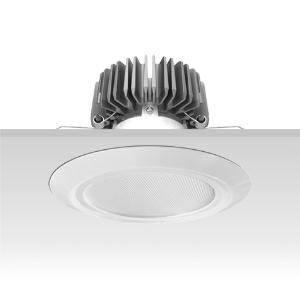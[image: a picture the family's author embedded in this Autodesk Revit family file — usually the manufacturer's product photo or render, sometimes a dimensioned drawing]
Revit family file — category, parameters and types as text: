
# Revit family: 3f_filippi_-_3f_reno_bianco_ampio_3f_filippi_-_30675_a01037_-_3f_reno_200_wh_2000-930_dali_wide___vs_wh_e44b
name_source: partatom
category: Lighting Fixtures
units: mm (PartAtom-declared; Revit-internal decimal feet)

## family parameters
Cut with Voids When Loaded = No
Host = Face
Light Source = No
Part Type = Normal
Room Calculation Point = No
Round Connector Dimension = Use Diameter
Shared = No

## types (1)
- 3F Filippi - 3F Reno Bianco Ampio (1 x LED, 1650 lm, 24 W, 3000 K)
    Apparent Load = 24 VA
    Approval mark = CE
    CIE Flux Codes = 75 94 99 100 100
    Color Rendering = 90
    Color Temperature = 3000 K
    Control Gear = Electronic transformer
    Default Elevation = 1800 mm
    Description = ILLUMINOTECHNICAL
Luminous efficiency 100% (DLOR 100%, ULOR 0%).
Initial luminous flux of the luminaire 1650 lm.
Direct symmetric wide distribution.
Installation Interdistance Transv.D = 1.16 x hu - Long.D = 1.14 x hu.
Average luminance <3000 cd/m² for radial angles >65°.
Tabular UGR (CIE 117 - 4H-8H; S=0.25H; 70/50/20): RUG 20.3 - 20.2.
Beam angle: 74° - 74°.
Luminous efficacy 69 lm/W.
Lifetime (L90/B10): 30000 h. (tq+25°C)
Lifetime (L85/B10): 50000 h. (tq+25°C)
Lifetime (L70/B10): 80000 h. (tq+25°C)
Sudden decreased luminous flux after 50000 hours: 0% (C0).
Photobiological safety in compliance with IEC/TR 62778: RG0 risk exempt, (IEC 62471).
In compliance with IEC/EN 62722-2-1 - IEC/EN 62717 standards.

SOURCE
Compact LED module 2000/930.
Energy efficiency class (UE 2019/2020 - UE 2019/2015): E.
CIE 13.3 Colour rendering index: CRI >90 (R9 >50%).
IES TM-30 Fidelity Index: Rf = 92 Rg = 101.
CCT nominal colour temperature 3000 K.
Colour initial tolerance (MacAdam): SDCM 3.
Zhaga Book 3 compliant.

MECHANICAL
Passive heat dissipator in die-casting aluminium, oversized, for optimum thermal management of the LED module.
Parabolic element with graduated/concentric rings in white polycarbonate.
Transparent external lens with glossy and satin differentiated surfaces, with a cooling and anti-insect system in methacrylate (PMMA).
Fastening spring clips in stainless steel.
Dimensions: diameter 226 mm, height 146 mm. Weight 1.195 kg.
IP44 protection degree for exposed part, IP20 for recessed part.
Mechanical strength to impacts IK06 (1 joule).
Glow-wire test resistance 650°C.

ELECTRICAL
Wiring on a separate unit.
Halogen Free DALI-2 DATI (Parts 251, 252, 253), PUSH-DIM, electronic wiring 230V-50/60Hz, power factor 0.95 at full load, THD <25%, constant output current, SELV, class II, 1 driver, 1 DALI addresse.
Power of the luminaire 24 W.
ENEC - CE.
SAFE FLICKER: PstLM=<1 and SVM=<0.4 (IEC TR 61547-1 and IEC TR 63158), to ensure a more comfortable and safe light.
Luminaire compliant with EN 60598-2-22 for power supply from a centralised emergency system CPSS (Central Power Supply System), not incorporated in the luminaire - high risk areas excluded. The default power and flux are 100% in AC and 100% in DC.
Ambient temperature from 0°C to +25°C.
Temperature class T6 max 85°C.
Relative humidity UR: <85%.

INSTALLATION
Pull-up recessed fitting.
False ceiling carving: 200 mm.
All accessories dedicated to this product are available on the Catalog and on our website www.3F-Filippi.com.

ACCESSORIES
A01037 - Anti-glare microprismatic VS moulded glass, tempered, not flammable, locked and in line with the trim, in white polycarbonate.

APPLICATIONS
Environments: architectural, commercial, exhibition areas, transit areas, corridors, shops, display windows, service areas.
In false ceilings with narrow voids.

LIGHT MANAGEMENT
Recommended minimum setting: 10%.
The luminaire, equipped with (DALI-2 DATI) driver, can be controlled manually with 3F Easy Dim technology or automatically/manually with wired or wireless DALI/D2D control systems.
The D2D driver guarantees interoperability with other devices with the same certification by making the following information available:
Device Data (Part 251), Energy Report (Part 252), Diagnosis & Maintenance (Part 253).
In electrical systems without a regulation system (manual or automatic) and DALI bus, a suitable jumper must be made on the DA-DA terminals of the appliance.

WARNING
Luminaire designed for disposal/recycling at end-of-life.
Replaceable (LED only) light source by a professional. Replaceable control gear by a professional.
    Height = 0 mm  [stored 0 ft]
    Lamp = 1 x LED
    Lamp Light Flux = 1650 lm
    Lamp Power = 24 W
    Lamp count = 1
    Length = 226 mm
    Lifetime = 50000 h
    Luminous efficacy = 69 lm/W
    Manufacturer = 3F Filippi
    ModVariant = No
    Model = 3F Filippi - 30675+A01037 - 3F Reno 200 WH 2000-930 DALI WIDE + VS WH
    Mounting Place = Ceiling
    Mounting Type = Recessed
    Number of Poles = 1
    OnlyDefault = Yes
    Power Factor = 1
    Product Name = 3F Filippi - 3F Reno Bianco Ampio
    Product group = recessed luminaire
    ProductGroupID = 4
    Protection Class = Protection class II
    Protection Degree = IP 20
    RLX_Detail_Level = 1
    RLX_Emergency_Light_Flux = 0 lm
    RLX_Emergency_Type = 0
    RLX_Emergency_Type_DB = No
    RlxData = <blob elided: 97125 chars, md5=a45fba65>
    Socket = socket
    Standby Power = 0 W
    System Light Flux = 1650 lm
    System Power = 24 W
    Type Comments = Product without accessories
    Type Image = 3ffilippi_3f_reno_200_wh_vs_smp.jpg
    URL = http://relux.com
    VarID = ---
    Voltage = 0 V
    Weight = 0.00 kg
    Width = 0 mm  [stored 0 ft]

note: [stored X ft] marks values corroborated as IEEE doubles in the binary element streams (Revit-internal decimal feet)

## geometry (parser evidence)
native form markers: Blend x4, Sweep x11
no freeform markers — native parametric forms only
